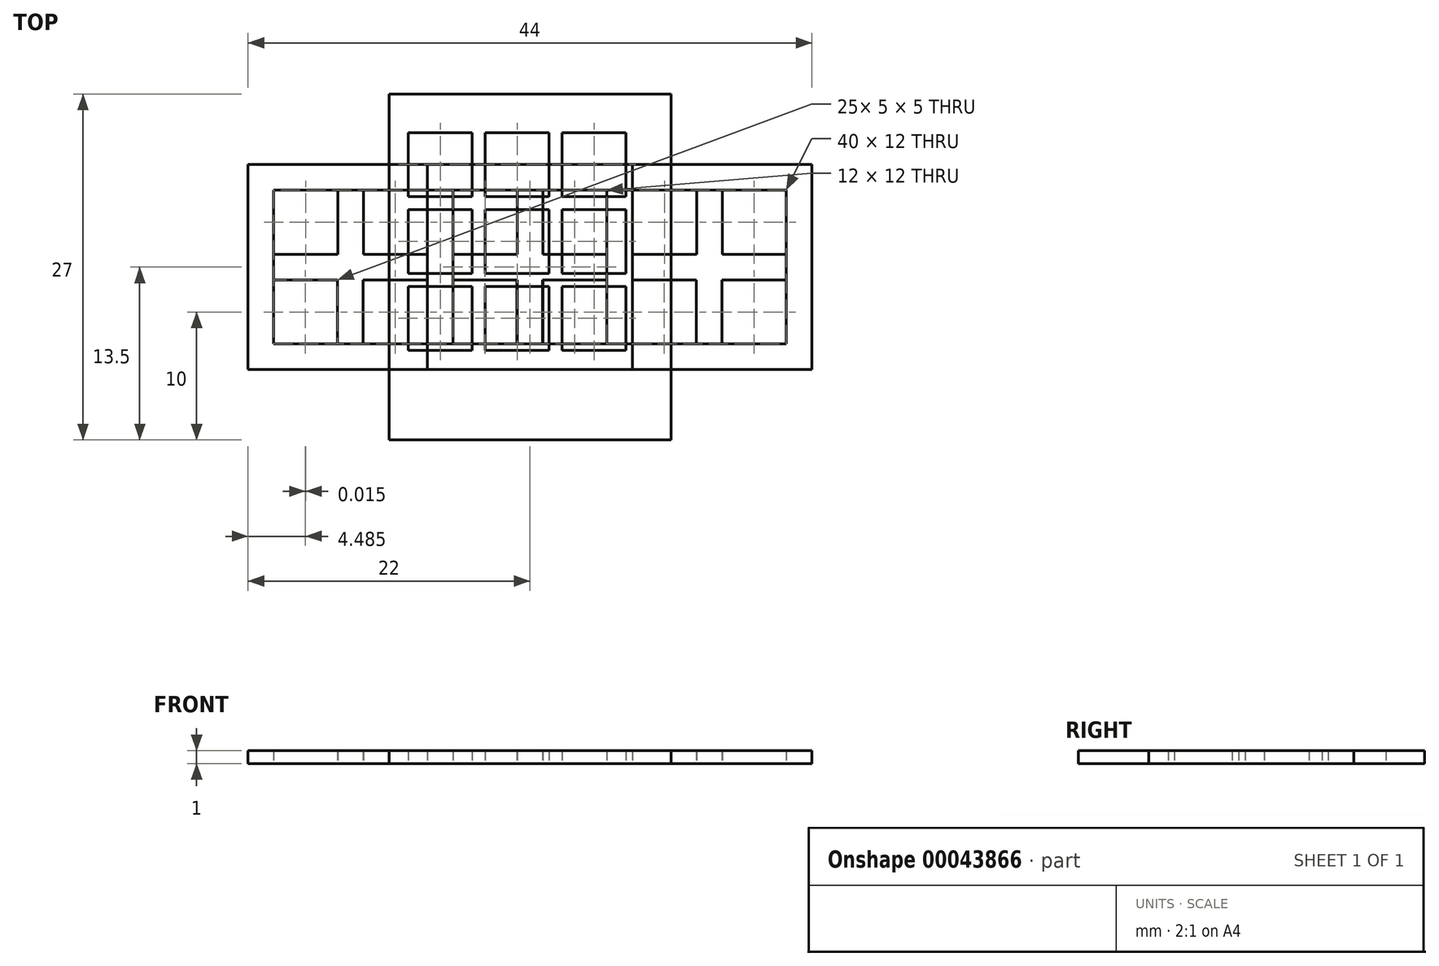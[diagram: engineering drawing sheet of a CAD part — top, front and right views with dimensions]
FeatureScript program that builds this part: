
annotation { "Feature Type Name" : "Feature", "Feature Type Description" : "" }
export const myFeature = defineFeature(function(context is Context, id is Id, definition is map)
    precondition{}
    {
        {
            var Q0;
            Q0=qCreatedBy(makeId("Top.planeOp"),FACE);
            var sketch = newSketch(context, id + "F0", { "sketchPlane" : qUnion([Q0])});
            skLineSegment(sketch, "E0.bottom", {"start": v(-8, -8) * mm, "end": v(8, -8) * mm});
            skLineSegment(sketch, "E0.top", {"start": v(-8, 8) * mm, "end": v(8, 8) * mm});
            skLineSegment(sketch, "E0.left", {"start": v(-8, -8) * mm, "end": v(-8, 8) * mm});
            skLineSegment(sketch, "E0.right", {"start": v(8, -8) * mm, "end": v(8, 8) * mm});
            skPoint(sketch, "E0.middle", {"position": v(0, 0) * mm});
            skLineSegment(sketch, "E1.bottom", {"start": v(6, 6) * mm, "end": v(-6, 6) * mm});
            skLineSegment(sketch, "E1.top", {"start": v(6, -6) * mm, "end": v(-6, -6) * mm});
            skLineSegment(sketch, "E1.left", {"start": v(6, 6) * mm, "end": v(6, -6) * mm});
            skLineSegment(sketch, "E1.right", {"start": v(-6, 6) * mm, "end": v(-6, -6) * mm});
            skSolve(sketch);
        }
        {
            var Q0;
            Q0=qCreatedBy(makeId("Top.planeOp"),FACE);
            var sketch = newSketch(context, id + "F1", { "sketchPlane" : qUnion([Q0])});
            skLineSegment(sketch, "E2.bottom", {"start": v(8, -8) * mm, "end": v(-8, -8) * mm});
            skLineSegment(sketch, "E2.top", {"start": v(8, 8) * mm, "end": v(-8, 8) * mm});
            skLineSegment(sketch, "E2.left", {"start": v(8, -8) * mm, "end": v(8, 8) * mm});
            skLineSegment(sketch, "E2.right", {"start": v(-8, -8) * mm, "end": v(-8, 8) * mm});
            skPoint(sketch, "E2.middle", {"position": v(0, 0) * mm});
            skLineSegment(sketch, "E3.bottom", {"start": v(-6, 6) * mm, "end": v(-1, 6) * mm});
            skLineSegment(sketch, "E3.top", {"start": v(-6, 1) * mm, "end": v(-1, 1) * mm});
            skLineSegment(sketch, "E3.left", {"start": v(-6, 6) * mm, "end": v(-6, 1) * mm});
            skLineSegment(sketch, "E3.right", {"start": v(-1, 6) * mm, "end": v(-1, 1) * mm});
            skLineSegment(sketch, "E4.1.0.0", {"start": v(1, 6) * mm, "end": v(1, 1) * mm});
            skLineSegment(sketch, "E4.1.0.1", {"start": v(1, 1) * mm, "end": v(6, 1) * mm});
            skLineSegment(sketch, "E4.1.0.2", {"start": v(6, 6) * mm, "end": v(6, 1) * mm});
            skLineSegment(sketch, "E4.1.0.3", {"start": v(1, 6) * mm, "end": v(6, 6) * mm});
            skLineSegment(sketch, "E4.direction1", {"start": v(-6, 1) * mm, "end": v(1, 1) * mm, "construction": true});
            skLineSegment(sketch, "E5.1.0.0", {"start": v(6, -1) * mm, "end": v(6, -6) * mm});
            skLineSegment(sketch, "E5.1.0.1", {"start": v(-1, -1) * mm, "end": v(-1, -6) * mm});
            skLineSegment(sketch, "E5.1.0.2", {"start": v(-6, -1) * mm, "end": v(-1, -1) * mm});
            skLineSegment(sketch, "E5.1.0.3", {"start": v(1, -1) * mm, "end": v(1, -6) * mm});
            skLineSegment(sketch, "E5.1.0.4", {"start": v(-6, -1) * mm, "end": v(-6, -6) * mm});
            skLineSegment(sketch, "E5.1.0.5", {"start": v(1, -1) * mm, "end": v(6, -1) * mm});
            skLineSegment(sketch, "E5.1.0.6", {"start": v(1, -6) * mm, "end": v(6, -6) * mm});
            skLineSegment(sketch, "E5.1.0.7", {"start": v(-6, -6) * mm, "end": v(-1, -6) * mm});
            skLineSegment(sketch, "E5.direction1", {"start": v(-6, 1) * mm, "end": v(-6, -6) * mm, "construction": true});
            skSolve(sketch);
        }
        {
            var Q0;
            Q0=qCreatedBy(makeId("Top.planeOp"),FACE);
            var sketch = newSketch(context, id + "F2", { "sketchPlane" : qUnion([Q0])});
            skLineSegment(sketch, "E6.bottom", {"start": v(22, -8) * mm, "end": v(-22, -8) * mm});
            skLineSegment(sketch, "E6.top", {"start": v(22, 8) * mm, "end": v(-22, 8) * mm});
            skLineSegment(sketch, "E6.left", {"start": v(22, -8) * mm, "end": v(22, 8) * mm});
            skLineSegment(sketch, "E6.right", {"start": v(-22, -8) * mm, "end": v(-22, 8) * mm});
            skPoint(sketch, "E6.middle", {"position": v(0, 0) * mm});
            skLineSegment(sketch, "E7.bottom", {"start": v(-20, 6) * mm, "end": v(-15, 6) * mm});
            skLineSegment(sketch, "E7.top", {"start": v(-20, 1) * mm, "end": v(-15, 1) * mm});
            skLineSegment(sketch, "E7.left", {"start": v(-20, 6) * mm, "end": v(-20, 1) * mm});
            skLineSegment(sketch, "E7.right", {"start": v(-15, 6) * mm, "end": v(-15, 1) * mm});
            skLineSegment(sketch, "E8.1.0.0", {"start": v(-13, 6) * mm, "end": v(-13, 1) * mm});
            skLineSegment(sketch, "E8.1.0.1", {"start": v(-13, 1) * mm, "end": v(-8, 1) * mm});
            skLineSegment(sketch, "E8.1.0.2", {"start": v(-8, 6) * mm, "end": v(-8, 1) * mm});
            skLineSegment(sketch, "E8.1.0.3", {"start": v(-13, 6) * mm, "end": v(-8, 6) * mm});
            skLineSegment(sketch, "E8.direction1", {"start": v(-20, 1) * mm, "end": v(-13, 1) * mm, "construction": true});
            skLineSegment(sketch, "E9.0.2.0", {"start": v(-6, 6) * mm, "end": v(-6, 1) * mm});
            skLineSegment(sketch, "E9.3.2.0", {"start": v(-6, 1) * mm, "end": v(-1, 1) * mm});
            skLineSegment(sketch, "E9.6.2.0", {"start": v(-1, 6) * mm, "end": v(-1, 1) * mm});
            skLineSegment(sketch, "E9.9.2.0", {"start": v(-6, 6) * mm, "end": v(-1, 6) * mm});
            skLineSegment(sketch, "E9.0.3.0", {"start": v(1, 6) * mm, "end": v(1, 1) * mm});
            skLineSegment(sketch, "E9.3.3.0", {"start": v(1, 1) * mm, "end": v(6, 1) * mm});
            skLineSegment(sketch, "E9.6.3.0", {"start": v(6, 6) * mm, "end": v(6, 1) * mm});
            skLineSegment(sketch, "E9.9.3.0", {"start": v(1, 6) * mm, "end": v(6, 6) * mm});
            skLineSegment(sketch, "E9.0.4.0", {"start": v(8, 6) * mm, "end": v(8, 1) * mm});
            skLineSegment(sketch, "E9.3.4.0", {"start": v(8, 1) * mm, "end": v(13, 1) * mm});
            skLineSegment(sketch, "E9.6.4.0", {"start": v(13, 6) * mm, "end": v(13, 1) * mm});
            skLineSegment(sketch, "E9.9.4.0", {"start": v(8, 6) * mm, "end": v(13, 6) * mm});
            skLineSegment(sketch, "E10.0.5.0", {"start": v(15, 6) * mm, "end": v(15, 1) * mm});
            skLineSegment(sketch, "E10.3.5.0", {"start": v(15, 1) * mm, "end": v(20, 1) * mm});
            skLineSegment(sketch, "E10.6.5.0", {"start": v(20, 6) * mm, "end": v(20, 1) * mm});
            skLineSegment(sketch, "E10.9.5.0", {"start": v(15, 6) * mm, "end": v(20, 6) * mm});
            skLineSegment(sketch, "E11.1.0.0", {"start": v(-13.01, -6) * mm, "end": v(-8.01, -6) * mm});
            skLineSegment(sketch, "E11.1.0.1", {"start": v(-13.01, -1) * mm, "end": v(-8.01, -1) * mm});
            skLineSegment(sketch, "E11.1.0.2", {"start": v(12.99, -1) * mm, "end": v(12.99, -6) * mm});
            skLineSegment(sketch, "E11.1.0.3", {"start": v(14.99, -1) * mm, "end": v(14.99, -6) * mm});
            skLineSegment(sketch, "E11.1.0.4", {"start": v(7.99, -1) * mm, "end": v(7.99, -6) * mm});
            skLineSegment(sketch, "E11.1.0.5", {"start": v(-20.01, -6) * mm, "end": v(-13.01, -6) * mm, "construction": true});
            skLineSegment(sketch, "E11.1.0.6", {"start": v(-20.01, -1) * mm, "end": v(-15.01, -1) * mm});
            skLineSegment(sketch, "E11.1.0.7", {"start": v(-1.01, -1) * mm, "end": v(-1.01, -6) * mm});
            skLineSegment(sketch, "E11.1.0.8", {"start": v(0.99, -1) * mm, "end": v(5.99, -1) * mm});
            skLineSegment(sketch, "E11.1.0.9", {"start": v(-13.01, -1) * mm, "end": v(-13.01, -6) * mm});
            skLineSegment(sketch, "E11.1.0.10", {"start": v(0.99, -1) * mm, "end": v(0.99, -6) * mm});
            skLineSegment(sketch, "E11.1.0.14", {"start": v(14.99, -1) * mm, "end": v(19.99, -1) * mm});
            skLineSegment(sketch, "E11.1.0.15", {"start": v(19.99, -1) * mm, "end": v(19.99, -6) * mm});
            skLineSegment(sketch, "E11.1.0.16", {"start": v(0.99, -6) * mm, "end": v(5.99, -6) * mm});
            skLineSegment(sketch, "E11.1.0.17", {"start": v(5.99, -1) * mm, "end": v(5.99, -6) * mm});
            skLineSegment(sketch, "E11.1.0.18", {"start": v(-6.01, -1) * mm, "end": v(-6.01, -6) * mm});
            skLineSegment(sketch, "E11.1.0.20", {"start": v(-6.01, -1) * mm, "end": v(-1.01, -1) * mm});
            skLineSegment(sketch, "E11.1.0.21", {"start": v(-8.01, -1) * mm, "end": v(-8.01, -6) * mm});
            skLineSegment(sketch, "E11.1.0.22", {"start": v(7.99, -1) * mm, "end": v(12.99, -1) * mm});
            skLineSegment(sketch, "E11.1.0.23", {"start": v(14.99, -6) * mm, "end": v(19.99, -6) * mm});
            skLineSegment(sketch, "E11.1.0.24", {"start": v(-20.01, -1) * mm, "end": v(-20.01, -6) * mm});
            skLineSegment(sketch, "E11.1.0.25", {"start": v(-6.01, -6) * mm, "end": v(-1.01, -6) * mm});
            skLineSegment(sketch, "E11.1.0.26", {"start": v(7.99, -6) * mm, "end": v(12.99, -6) * mm});
            skLineSegment(sketch, "E11.1.0.27", {"start": v(-15.01, -1) * mm, "end": v(-15.01, -6) * mm});
            skLineSegment(sketch, "E11.1.0.28", {"start": v(-20.01, -6) * mm, "end": v(-15.01, -6) * mm});
            skLineSegment(sketch, "E11.direction1", {"start": v(-20, 1) * mm, "end": v(-20.01, -6) * mm, "construction": true});
            skSolve(sketch);
        }
        {
            var Q0;
            Q0=qCreatedBy(makeId("Top.planeOp"),FACE);
            var sketch = newSketch(context, id + "F3", { "sketchPlane" : qUnion([Q0])});
            skLineSegment(sketch, "E12.bottom", {"start": v(-22, -8) * mm, "end": v(22, -8) * mm});
            skLineSegment(sketch, "E12.top", {"start": v(-22, 8) * mm, "end": v(22, 8) * mm});
            skLineSegment(sketch, "E12.left", {"start": v(-22, -8) * mm, "end": v(-22, 8) * mm});
            skLineSegment(sketch, "E12.right", {"start": v(22, -8) * mm, "end": v(22, 8) * mm});
            skPoint(sketch, "E12.middle", {"position": v(0, 0) * mm});
            skLineSegment(sketch, "E13.bottom", {"start": v(20, 6) * mm, "end": v(-20, 6) * mm});
            skLineSegment(sketch, "E13.top", {"start": v(20, -6) * mm, "end": v(-20, -6) * mm});
            skLineSegment(sketch, "E13.left", {"start": v(20, 6) * mm, "end": v(20, -6) * mm});
            skLineSegment(sketch, "E13.right", {"start": v(-20, 6) * mm, "end": v(-20, -6) * mm});
            skSolve(sketch);
        }
        {
            var Q0;
            Q0 = qSketchRegion(id + "F1", true);
            extrude(context, id + "F4", {"entities" : qUnion([Q0]), "depth" : 1 * mm, "offsetDistance" : 25 * mm});
        }
        {
            var Q0;
            Q0=makeQuery(id+"F0.imprint","IMPRINT",FACE,{"disambiguationData":[TD([[makeQuery(id+"F0.imprint","IMPRINT",EDGE,{"derivedFrom":sQuery(id+"F0.wireOp",EDGE,"E0.bottom")}),1.0]])]});
            extrude(context, id + "F5", {"entities" : qUnion([Q0]), "depth" : 1 * mm, "offsetDistance" : 25 * mm});
        }
        {
            var Q0;
            Q0 = qSketchRegion(id + "F2", true);
            extrude(context, id + "F6", {"entities" : qUnion([Q0]), "depth" : 1 * mm, "offsetDistance" : 25 * mm});
        }
        {
            var Q0;
            Q0 = qSketchRegion(id + "F3", true);
            extrude(context, id + "F7", {"entities" : qUnion([Q0]), "depth" : 1 * mm, "offsetDistance" : 25 * mm});
        }
        {
            var Q0;
            Q0=qCreatedBy(makeId("Top.planeOp"),FACE);
            var sketch = newSketch(context, id + "F8", { "sketchPlane" : qUnion([Q0])});
            skLineSegment(sketch, "E14.bottom", {"start": v(11, -13.5) * mm, "end": v(-11, -13.5) * mm});
            skLineSegment(sketch, "E14.top", {"start": v(11, 13.5) * mm, "end": v(-11, 13.5) * mm});
            skLineSegment(sketch, "E14.left", {"start": v(11, -13.5) * mm, "end": v(11, 13.5) * mm});
            skLineSegment(sketch, "E14.right", {"start": v(-11, -13.5) * mm, "end": v(-11, 13.5) * mm});
            skPoint(sketch, "E14.middle", {"position": v(0, 0) * mm});
            skLineSegment(sketch, "E15.bottom", {"start": v(-9.5, 10.5) * mm, "end": v(-4.5, 10.5) * mm});
            skLineSegment(sketch, "E15.top", {"start": v(-9.5, 5.5) * mm, "end": v(-4.5, 5.5) * mm});
            skLineSegment(sketch, "E15.left", {"start": v(-9.5, 10.5) * mm, "end": v(-9.5, 5.5) * mm});
            skLineSegment(sketch, "E15.right", {"start": v(-4.5, 10.5) * mm, "end": v(-4.5, 5.5) * mm});
            skLineSegment(sketch, "E16.bottom", {"start": v(-11, -13.5) * mm, "end": v(9, -13.5) * mm, "construction": true});
            skLineSegment(sketch, "E16.top", {"start": v(-11, 11.5) * mm, "end": v(9, 11.5) * mm, "construction": true});
            skLineSegment(sketch, "E16.left", {"start": v(-11, -13.5) * mm, "end": v(-11, 11.5) * mm, "construction": true});
            skLineSegment(sketch, "E16.right", {"start": v(9, -13.5) * mm, "end": v(9, 11.5) * mm, "construction": true});
            skLineSegment(sketch, "E17.1.0.0", {"start": v(-3.5, 10.5) * mm, "end": v(1.5, 10.5) * mm});
            skLineSegment(sketch, "E17.1.0.1", {"start": v(-3.5, 10.5) * mm, "end": v(-3.5, 5.5) * mm});
            skLineSegment(sketch, "E17.1.0.2", {"start": v(-3.5, 5.5) * mm, "end": v(1.5, 5.5) * mm});
            skLineSegment(sketch, "E17.1.0.3", {"start": v(1.5, 10.5) * mm, "end": v(1.5, 5.5) * mm});
            skLineSegment(sketch, "E17.2.0.0", {"start": v(2.5, 10.5) * mm, "end": v(7.5, 10.5) * mm});
            skLineSegment(sketch, "E17.2.0.1", {"start": v(2.5, 10.5) * mm, "end": v(2.5, 5.5) * mm});
            skLineSegment(sketch, "E17.2.0.2", {"start": v(2.5, 5.5) * mm, "end": v(7.5, 5.5) * mm});
            skLineSegment(sketch, "E17.2.0.3", {"start": v(7.5, 10.5) * mm, "end": v(7.5, 5.5) * mm});
            skLineSegment(sketch, "E17.direction1", {"start": v(-9, 6.5) * mm, "end": v(-3, 6.5) * mm, "construction": true});
            skLineSegment(sketch, "E18.1.0.0", {"start": v(2.5, -0.5) * mm, "end": v(7.5, -0.5) * mm});
            skLineSegment(sketch, "E18.1.0.1", {"start": v(-9.5, 4.5) * mm, "end": v(-4.5, 4.5) * mm});
            skLineSegment(sketch, "E18.1.0.2", {"start": v(-9.5, 4.5) * mm, "end": v(-9.5, -0.5) * mm});
            skLineSegment(sketch, "E18.1.0.3", {"start": v(-3.5, 4.5) * mm, "end": v(1.5, 4.5) * mm});
            skLineSegment(sketch, "E18.1.0.4", {"start": v(1.5, 4.5) * mm, "end": v(1.5, -0.5) * mm});
            skLineSegment(sketch, "E18.1.0.5", {"start": v(-9, 0.5) * mm, "end": v(-3, 0.5) * mm, "construction": true});
            skLineSegment(sketch, "E18.1.0.6", {"start": v(-3.5, 4.5) * mm, "end": v(-3.5, -0.5) * mm});
            skLineSegment(sketch, "E18.1.0.7", {"start": v(-4.5, 4.5) * mm, "end": v(-4.5, -0.5) * mm});
            skLineSegment(sketch, "E18.1.0.8", {"start": v(2.5, 4.5) * mm, "end": v(7.5, 4.5) * mm});
            skLineSegment(sketch, "E18.1.0.9", {"start": v(-9.5, -0.5) * mm, "end": v(-4.5, -0.5) * mm});
            skLineSegment(sketch, "E18.1.0.10", {"start": v(7.5, 4.5) * mm, "end": v(7.5, -0.5) * mm});
            skLineSegment(sketch, "E18.1.0.11", {"start": v(2.5, 4.5) * mm, "end": v(2.5, -0.5) * mm});
            skLineSegment(sketch, "E18.1.0.12", {"start": v(-3.5, -0.5) * mm, "end": v(1.5, -0.5) * mm});
            skLineSegment(sketch, "E18.2.0.0", {"start": v(2.5, -6.5) * mm, "end": v(7.5, -6.5) * mm});
            skLineSegment(sketch, "E18.2.0.1", {"start": v(-9.5, -1.5) * mm, "end": v(-4.5, -1.5) * mm});
            skLineSegment(sketch, "E18.2.0.2", {"start": v(-9.5, -1.5) * mm, "end": v(-9.5, -6.5) * mm});
            skLineSegment(sketch, "E18.2.0.3", {"start": v(-3.5, -1.5) * mm, "end": v(1.5, -1.5) * mm});
            skLineSegment(sketch, "E18.2.0.4", {"start": v(1.5, -1.5) * mm, "end": v(1.5, -6.5) * mm});
            skLineSegment(sketch, "E18.2.0.5", {"start": v(-9, -5.5) * mm, "end": v(-3, -5.5) * mm, "construction": true});
            skLineSegment(sketch, "E18.2.0.6", {"start": v(-3.5, -1.5) * mm, "end": v(-3.5, -6.5) * mm});
            skLineSegment(sketch, "E18.2.0.7", {"start": v(-4.5, -1.5) * mm, "end": v(-4.5, -6.5) * mm});
            skLineSegment(sketch, "E18.2.0.8", {"start": v(2.5, -1.5) * mm, "end": v(7.5, -1.5) * mm});
            skLineSegment(sketch, "E18.2.0.9", {"start": v(-9.5, -6.5) * mm, "end": v(-4.5, -6.5) * mm});
            skLineSegment(sketch, "E18.2.0.10", {"start": v(7.5, -1.5) * mm, "end": v(7.5, -6.5) * mm});
            skLineSegment(sketch, "E18.2.0.11", {"start": v(2.5, -1.5) * mm, "end": v(2.5, -6.5) * mm});
            skLineSegment(sketch, "E18.2.0.12", {"start": v(-3.5, -6.5) * mm, "end": v(1.5, -6.5) * mm});
            skLineSegment(sketch, "E18.direction1", {"start": v(-9.5, 5.5) * mm, "end": v(-9.5, -0.5) * mm, "construction": true});
            skSolve(sketch);
        }
        {
            var Q0;
            Q0 = qSketchRegion(id + "F8", true);
            extrude(context, id + "F9", {"entities" : qUnion([Q0]), "depth" : 1 * mm, "offsetDistance" : 25 * mm});
        }
    });
